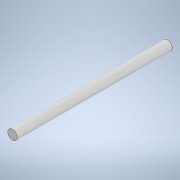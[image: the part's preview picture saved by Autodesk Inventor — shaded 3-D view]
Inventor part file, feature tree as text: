
AUTODESK INVENTOR PART (.ipt)
format: ipt  version: 2020.3 (Build 243373000, 373)  size: 90,624 bytes
history: native  units: mm
features: extrude x1, sketch x1
ambient origin geometry x8: Origin, YZ Plane, XZ Plane, XY Plane, X Axis, Y Axis, Z Axis, Center Point
bodies: Solid1 (feature_tree)
feature tree (2):
  extrude  "Extrusion1"  Depth=130.0mm TaperAngle=0.0deg
  sketch  "Sketch1"  dims[d0=8.0mm d1=130.0mm d2=0.0mm]
